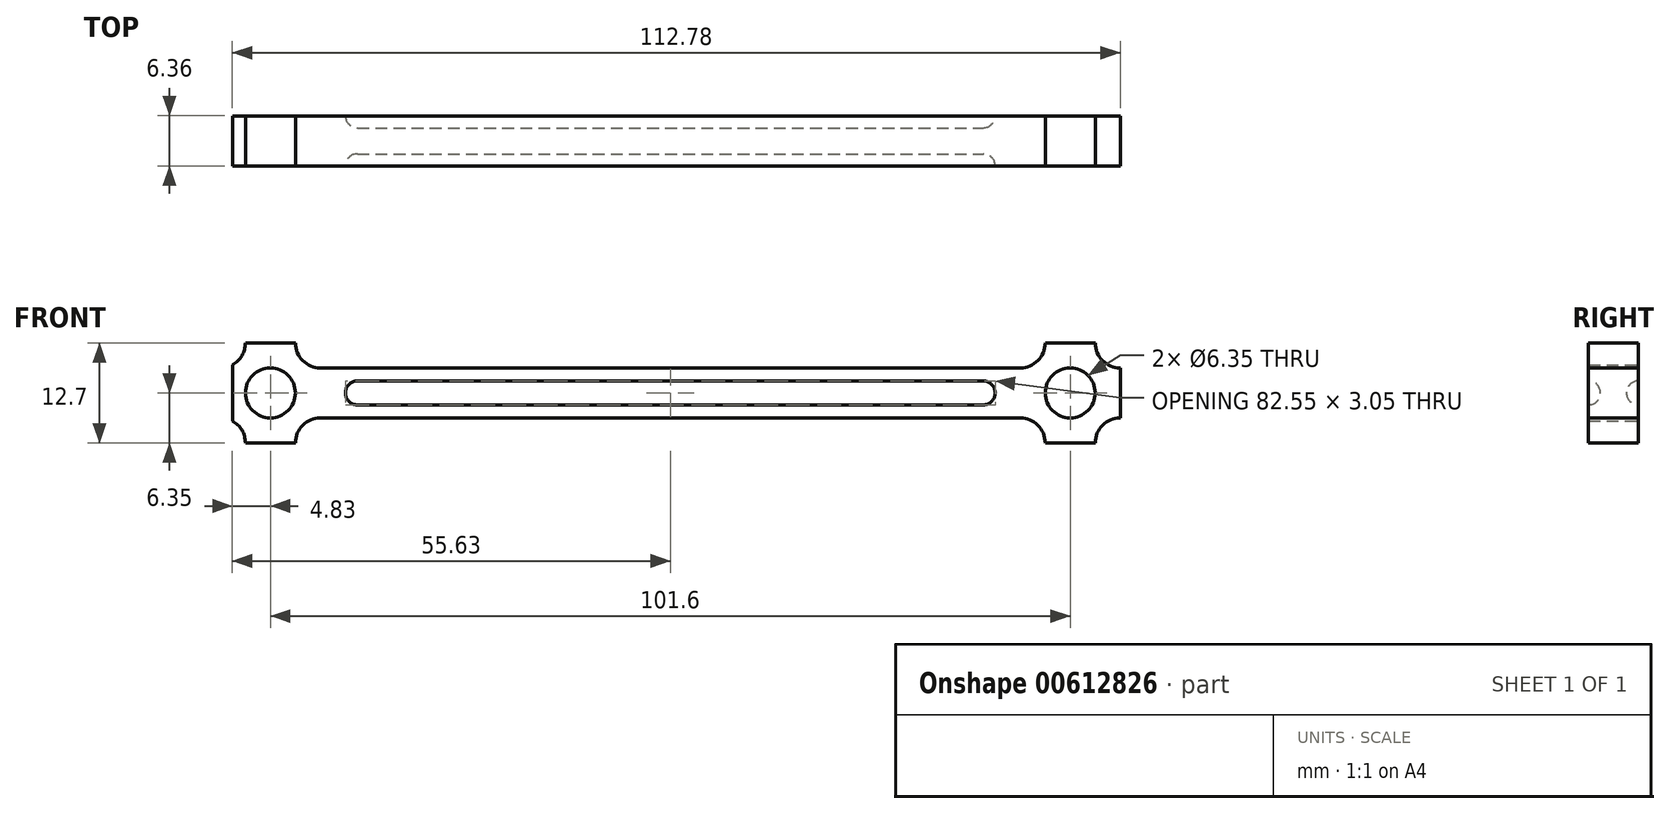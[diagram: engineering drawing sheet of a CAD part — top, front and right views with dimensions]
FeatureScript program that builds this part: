
annotation { "Feature Type Name" : "Feature", "Feature Type Description" : "" }
export const myFeature = defineFeature(function(context is Context, id is Id, definition is map)
    precondition{}
    {
        {
            var Q0;
            Q0=qCreatedBy(makeId("Front.planeOp"),FACE);
            var sketch = newSketch(context, id + "F0", { "sketchPlane" : qUnion([Q0])});
            skLineSegment(sketch, "E0", {"start": v(-44.45, 3.17) * mm, "end": v(44.45, 3.17) * mm});
            skArc(sketch, "E1", {"start": v(44.45, 3.17) * mm, "mid": v(46.7, 4.1) * mm, "end": v(47.63, 6.35) * mm});
            skLineSegment(sketch, "E2", {"start": v(47.62, 6.35) * mm, "end": v(53.98, 6.35) * mm});
            skLineSegment(sketch, "E3", {"start": v(57.15, 3.18) * mm, "end": v(57.15, -3.18) * mm});
            skLineSegment(sketch, "E4", {"start": v(53.98, -6.35) * mm, "end": v(47.62, -6.35) * mm});
            skLineSegment(sketch, "E5", {"start": v(44.45, -3.18) * mm, "end": v(-44.45, -3.18) * mm});
            skCircle(sketch, "E6", {"center": v(50.8, 0) * mm, "radius": 3.18 * mm});
            skCircle(sketch, "E7", {"center": v(-50.8, 0) * mm, "radius": 3.18 * mm});
            skPoint(sketch, "E8", {"position": v(0, 3.18) * mm});
            skPoint(sketch, "E9", {"position": v(57.15, 0) * mm});
            skArc(sketch, "E10", {"start": v(53.98, 6.35) * mm, "mid": v(54.9, 4.1) * mm, "end": v(57.15, 3.17) * mm});
            skPoint(sketch, "E11", {"position": v(50.8, 6.35) * mm});
            skPoint(sketch, "E12", {"position": v(50.8, -6.35) * mm});
            skArc(sketch, "E13", {"start": v(47.63, -6.35) * mm, "mid": v(46.7, -4.1) * mm, "end": v(44.45, -3.18) * mm});
            skArc(sketch, "E14", {"start": v(57.15, -3.17) * mm, "mid": v(54.9, -4.1) * mm, "end": v(53.98, -6.35) * mm});
            skArc(sketch, "E15", {"start": v(-47.62, 6.35) * mm, "mid": v(-46.7, 4.1) * mm, "end": v(-44.45, 3.18) * mm});
            skArc(sketch, "E16", {"start": v(-44.45, -3.18) * mm, "mid": v(-46.7, -4.1) * mm, "end": v(-47.62, -6.35) * mm});
            skLineSegment(sketch, "E17", {"start": v(-47.62, 6.35) * mm, "end": v(-53.97, 6.35) * mm});
            skLineSegment(sketch, "E18", {"start": v(-47.62, -6.35) * mm, "end": v(-53.97, -6.35) * mm});
            skArc(sketch, "E19", {"start": v(-55.63, 3.56) * mm, "mid": v(-54.42, 4.73) * mm, "end": v(-53.97, 6.35) * mm});
            skArc(sketch, "E20", {"start": v(-53.97, -6.35) * mm, "mid": v(-54.42, -4.73) * mm, "end": v(-55.63, -3.56) * mm});
            skPoint(sketch, "E21", {"position": v(-50.8, 6.35) * mm});
            skLineSegment(sketch, "E22", {"start": v(-55.63, 3.56) * mm, "end": v(-55.63, -3.56) * mm});
            skPoint(sketch, "E23.orphan", {"position": v(-57.15, 3.18) * mm});
            skPoint(sketch, "E24.orphan", {"position": v(-57.15, -3.18) * mm});
            skSolve(sketch);
        }
        {
            var Q0;
            Q0=qSketchRegion(id+"F0",true);
            extrude(context, id + "F1", {"entities" : qUnion([Q0]), "depth" : 6.35 * mm, "symmetric" : true});
        }
        {
            var Q0;
            Q0=qCreatedBy(makeId("Right.planeOp"),FACE);
            var sketch = newSketch(context, id + "F2", { "sketchPlane" : qUnion([Q0])});
            skArc(sketch, "E25", {"start": v(3.17, 1.52) * mm, "mid": v(1.65, 0) * mm, "end": v(3.18, -1.52) * mm});
            skArc(sketch, "E26", {"start": v(-3.18, -1.52) * mm, "mid": v(-1.65, 0) * mm, "end": v(-3.18, 1.52) * mm});
            skLineSegment(sketch, "E27", {"start": v(3.18, -1.52) * mm, "end": v(3.17, 1.52) * mm});
            skLineSegment(sketch, "E28", {"start": v(-3.18, -1.52) * mm, "end": v(-3.18, 1.52) * mm});
            skSolve(sketch);
        }
        {
            var Q0;
            Q0=qSketchRegion(id+"F2",true);
            extrude(context, id + "F3", {"entities" : qUnion([Q0]), "operationType" : NewBodyOperationType.REMOVE, "oppositeDirection" : true, "depth" : 82.55 * mm, "symmetric" : true});
        }
        {
            var Q0;
            Q0=makeQuery(id+"F3.boolean.opBoolean","COPY",EDGE,{"derivedFrom":makeQuery(id+"F3.opExtrude","CAP_EDGE",EDGE,{"disambiguationData":[OSD([sQuery(id+"F2.wireOp",EDGE,"E25")])],"isStart":true})});
            var Q1;
            Q1=makeQuery(id+"F3.boolean.opBoolean","COPY",EDGE,{"derivedFrom":makeQuery(id+"F3.opExtrude","CAP_EDGE",EDGE,{"disambiguationData":[OSD([sQuery(id+"F2.wireOp",EDGE,"E25")])],"isStart":false})});
            var Q2;
            Q2=makeQuery(id+"F3.boolean.opBoolean","COPY",EDGE,{"derivedFrom":makeQuery(id+"F3.opExtrude","CAP_EDGE",EDGE,{"disambiguationData":[OSD([sQuery(id+"F2.wireOp",EDGE,"E26")])],"isStart":false})});
            var Q3;
            Q3=makeQuery(id+"F3.boolean.opBoolean","COPY",EDGE,{"derivedFrom":makeQuery(id+"F3.opExtrude","CAP_EDGE",EDGE,{"disambiguationData":[OSD([sQuery(id+"F2.wireOp",EDGE,"E26")])],"isStart":true})});
            fillet(context, id + "F4", {"entities" : qUnion([Q0, Q1, Q2, Q3]), "radius" : 1.52 * mm, "tangentPropagation" : true, "allowEdgeOverflow" : false});
        }
    });
